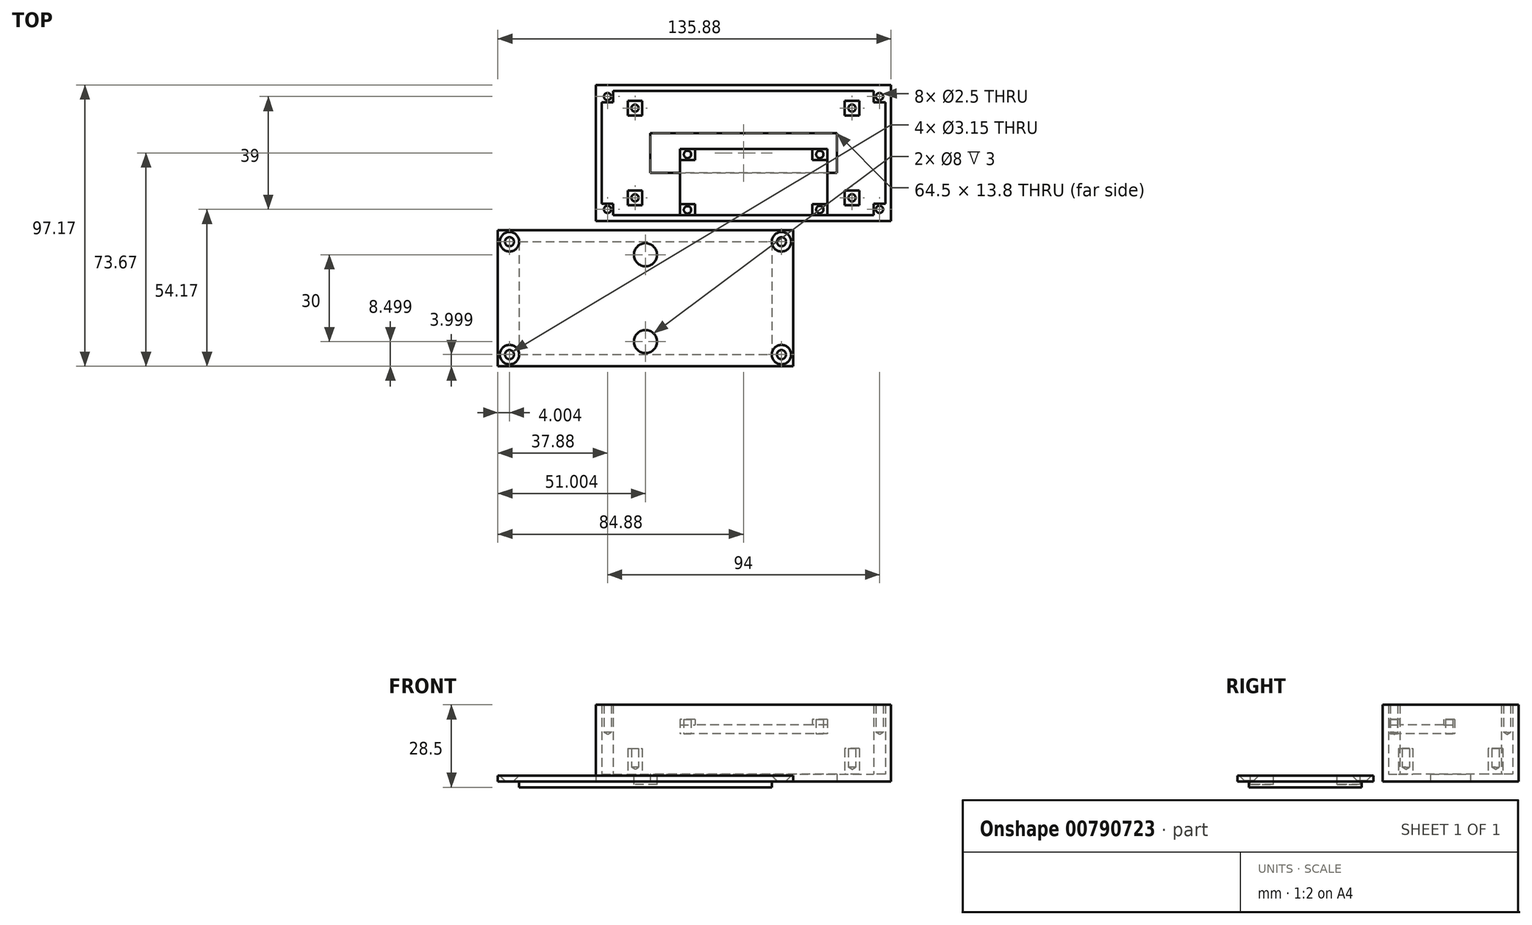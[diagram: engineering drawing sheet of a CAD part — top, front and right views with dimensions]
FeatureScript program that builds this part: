
annotation { "Feature Type Name" : "Feature", "Feature Type Description" : "" }
export const myFeature = defineFeature(function(context is Context, id is Id, definition is map)
    precondition{}
    {
        {
            var Q0;
            Q0=qCreatedBy(makeId("Top.planeOp"),FACE);
            var sketch = newSketch(context, id + "F0", { "sketchPlane" : qUnion([Q0])});
            skLineSegment(sketch, "E0.bottom", {"start": v(-51, 23.5) * mm, "end": v(51, 23.5) * mm});
            skLineSegment(sketch, "E0.top", {"start": v(-51, -23.5) * mm, "end": v(51, -23.5) * mm});
            skLineSegment(sketch, "E0.left", {"start": v(-51, 23.5) * mm, "end": v(-51, -23.5) * mm});
            skLineSegment(sketch, "E0.right", {"start": v(51, 23.5) * mm, "end": v(51, -23.5) * mm});
            skPoint(sketch, "E0.middle", {"position": v(0, 0) * mm});
            skSolve(sketch);
        }
        {
            var Q0;
            Q0=makeQuery(id+"F0.imprint","IMPRINT",FACE,{"disambiguationData":[TD([[makeQuery(id+"F0.imprint","IMPRINT",EDGE,{"derivedFrom":sQuery(id+"F0.wireOp",EDGE,"E0.bottom")}),-1.0]])]});
            extrude(context, id + "F1", {"entities" : qUnion([Q0]), "depth" : 26.5 * mm, "offsetDistance" : 25 * mm});
        }
        {
            var Q0;
            Q0=makeQuery(id+"F1.opExtrude","CAP_FACE",FACE,{"disambiguationData":[OSD([sQuery(id+"F0.wireOp",EDGE,"E0.bottom"),sQuery(id+"F0.wireOp",EDGE,"E0.top"),sQuery(id+"F0.wireOp",EDGE,"E0.left"),sQuery(id+"F0.wireOp",EDGE,"E0.right")])],"isStart":false});
            var sketch = newSketch(context, id + "F2", { "sketchPlane" : qUnion([Q0])});
            skLineSegment(sketch, "E1.bottom", {"start": v(-49, 21.5) * mm, "end": v(49, 21.5) * mm});
            skLineSegment(sketch, "E1.top", {"start": v(-49, -21.5) * mm, "end": v(49, -21.5) * mm});
            skLineSegment(sketch, "E1.left", {"start": v(-49, 21.5) * mm, "end": v(-49, -21.5) * mm});
            skLineSegment(sketch, "E1.right", {"start": v(49, 21.5) * mm, "end": v(49, -21.5) * mm});
            skPoint(sketch, "E1.middle", {"position": v(0, 0) * mm});
            skSolve(sketch);
        }
        {
            var Q0;
            Q0=makeQuery(id+"F2.imprint","IMPRINT",FACE,{"disambiguationData":[TD([[makeQuery(id+"F2.imprint","IMPRINT",EDGE,{"derivedFrom":sQuery(id+"F2.wireOp",EDGE,"E1.bottom")}),-1.0]])]});
            extrude(context, id + "F3", {"entities" : qUnion([Q0]), "operationType" : NewBodyOperationType.REMOVE, "oppositeDirection" : true, "depth" : 24 * mm, "offsetDistance" : 25 * mm});
        }
        {
            var Q0;
            Q0=makeQuery(id+"F1.opExtrude","CAP_FACE",FACE,{"disambiguationData":[OSD([sQuery(id+"F0.wireOp",EDGE,"E0.bottom"),sQuery(id+"F0.wireOp",EDGE,"E0.top"),sQuery(id+"F0.wireOp",EDGE,"E0.left"),sQuery(id+"F0.wireOp",EDGE,"E0.right")])],"isStart":true});
            var sketch = newSketch(context, id + "F4", { "sketchPlane" : qUnion([Q0])});
            skLineSegment(sketch, "E2.bottom", {"start": v(-32.25, -6.9) * mm, "end": v(32.25, -6.9) * mm});
            skLineSegment(sketch, "E2.top", {"start": v(-32.25, 6.9) * mm, "end": v(32.25, 6.9) * mm});
            skLineSegment(sketch, "E2.left", {"start": v(-32.25, -6.9) * mm, "end": v(-32.25, 6.9) * mm});
            skLineSegment(sketch, "E2.right", {"start": v(32.25, -6.9) * mm, "end": v(32.25, 6.9) * mm});
            skPoint(sketch, "E2.middle", {"position": v(0, 0) * mm});
            skSolve(sketch);
        }
        {
            var Q0;
            Q0=makeQuery(id+"F4.imprint","IMPRINT",FACE,{"disambiguationData":[TD([[makeQuery(id+"F4.imprint","IMPRINT",EDGE,{"derivedFrom":sQuery(id+"F4.wireOp",EDGE,"E2.bottom")}),1.0]])]});
            extrude(context, id + "F5", {"entities" : qUnion([Q0]), "operationType" : NewBodyOperationType.REMOVE, "endBound" : BoundingType.THROUGH_ALL, "oppositeDirection" : true, "depth" : 25 * mm, "offsetDistance" : 25 * mm});
        }
        {
            var Q0;
            Q0=makeQuery(id+"F3.boolean.opBoolean","COPY",FACE,{"derivedFrom":makeQuery(id+"F3.opExtrude","CAP_FACE",FACE,{"disambiguationData":[OSD([sQuery(id+"F2.wireOp",EDGE,"E1.bottom"),sQuery(id+"F2.wireOp",EDGE,"E1.top"),sQuery(id+"F2.wireOp",EDGE,"E1.left"),sQuery(id+"F2.wireOp",EDGE,"E1.right")])],"isStart":false})});
            var sketch = newSketch(context, id + "F6", { "sketchPlane" : qUnion([Q0])});
            skLineSegment(sketch, "E3.bottom", {"start": v(-40, 18) * mm, "end": v(40, 18) * mm, "construction": true});
            skLineSegment(sketch, "E3.top", {"start": v(-40, -18) * mm, "end": v(40, -18) * mm, "construction": true});
            skLineSegment(sketch, "E3.left", {"start": v(-40, 18) * mm, "end": v(-40, -18) * mm, "construction": true});
            skLineSegment(sketch, "E3.right", {"start": v(40, 18) * mm, "end": v(40, -18) * mm, "construction": true});
            skPoint(sketch, "E3.middle", {"position": v(0, 0) * mm});
            skLineSegment(sketch, "E4.bottom", {"start": v(-40, -18) * mm, "end": v(-35, -18) * mm});
            skLineSegment(sketch, "E4.top", {"start": v(-40, -13) * mm, "end": v(-35, -13) * mm});
            skLineSegment(sketch, "E4.left", {"start": v(-40, -18) * mm, "end": v(-40, -13) * mm});
            skLineSegment(sketch, "E4.right", {"start": v(-35, -18) * mm, "end": v(-35, -13) * mm});
            skLineSegment(sketch, "E5.bottom", {"start": v(-40, 18) * mm, "end": v(-35, 18) * mm});
            skLineSegment(sketch, "E5.top", {"start": v(-40, 13) * mm, "end": v(-35, 13) * mm});
            skLineSegment(sketch, "E5.left", {"start": v(-40, 18) * mm, "end": v(-40, 13) * mm});
            skLineSegment(sketch, "E5.right", {"start": v(-35, 18) * mm, "end": v(-35, 13) * mm});
            skLineSegment(sketch, "E6.bottom", {"start": v(40, 18) * mm, "end": v(35, 18) * mm});
            skLineSegment(sketch, "E6.top", {"start": v(40, 13) * mm, "end": v(35, 13) * mm});
            skLineSegment(sketch, "E6.left", {"start": v(40, 18) * mm, "end": v(40, 13) * mm});
            skLineSegment(sketch, "E6.right", {"start": v(35, 18) * mm, "end": v(35, 13) * mm});
            skLineSegment(sketch, "E7.bottom", {"start": v(40, -18) * mm, "end": v(35, -18) * mm});
            skLineSegment(sketch, "E7.top", {"start": v(40, -13) * mm, "end": v(35, -13) * mm});
            skLineSegment(sketch, "E7.left", {"start": v(40, -18) * mm, "end": v(40, -13) * mm});
            skLineSegment(sketch, "E7.right", {"start": v(35, -18) * mm, "end": v(35, -13) * mm});
            skPoint(sketch, "E8.centerSnap0", {"position": v(-40, 15.5) * mm});
            skPoint(sketch, "E8.centerSnap1", {"position": v(-37.5, 18) * mm});
            skPoint(sketch, "E9.centerSnap0", {"position": v(-40, -15.5) * mm});
            skPoint(sketch, "E9.centerSnap1", {"position": v(-37.5, -13) * mm});
            skPoint(sketch, "E10.centerSnap0", {"position": v(35, -15.5) * mm});
            skPoint(sketch, "E10.centerSnap1", {"position": v(37.5, -13) * mm});
            skPoint(sketch, "E11.centerSnap0", {"position": v(37.5, 13) * mm});
            skPoint(sketch, "E11.centerSnap1", {"position": v(35, 15.5) * mm});
            skSolve(sketch);
        }
        {
            var Q0;
            Q0=makeQuery(id+"F6.imprint","IMPRINT",FACE,{"disambiguationData":[TD([[makeQuery(id+"F6.imprint","IMPRINT",EDGE,{"derivedFrom":sQuery(id+"F6.wireOp",EDGE,"E5.bottom")}),-1.0]])]});
            var Q1;
            Q1=makeQuery(id+"F6.imprint","IMPRINT",FACE,{"disambiguationData":[TD([[makeQuery(id+"F6.imprint","IMPRINT",EDGE,{"derivedFrom":sQuery(id+"F6.wireOp",EDGE,"E4.bottom")}),1.0]])]});
            var Q2;
            Q2=makeQuery(id+"F6.imprint","IMPRINT",FACE,{"disambiguationData":[TD([[makeQuery(id+"F6.imprint","IMPRINT",EDGE,{"derivedFrom":sQuery(id+"F6.wireOp",EDGE,"E7.bottom")}),-1.0]])]});
            var Q3;
            Q3=makeQuery(id+"F6.imprint","IMPRINT",FACE,{"disambiguationData":[TD([[makeQuery(id+"F6.imprint","IMPRINT",EDGE,{"derivedFrom":sQuery(id+"F6.wireOp",EDGE,"E6.bottom")}),1.0]])]});
            extrude(context, id + "F7", {"entities" : qUnion([Q0, Q1, Q2, Q3]), "operationType" : NewBodyOperationType.ADD, "depth" : 8.9 * mm, "offsetDistance" : 25 * mm});
        }
        {
            var Q0;
            Q0=makeQuery(id+"F7.opExtrude","CAP_FACE",FACE,{"disambiguationData":[OSD([sQuery(id+"F6.wireOp",EDGE,"E5.bottom"),sQuery(id+"F6.wireOp",EDGE,"E5.top"),sQuery(id+"F6.wireOp",EDGE,"E5.left"),sQuery(id+"F6.wireOp",EDGE,"E5.right")])],"isStart":false});
            var sketch = newSketch(context, id + "F8", { "sketchPlane" : qUnion([Q0])});
            skPoint(sketch, "E12", {"position": v(-37.5, 15.5) * mm});
            skPoint(sketch, "E12.positionSnap0", {"position": v(-40, 15.5) * mm});
            skPoint(sketch, "E12.positionSnap1", {"position": v(-37.5, 18) * mm});
            skSolve(sketch);
        }
        {
            var Q0;
            Q0=makeQuery(id+"F7.opExtrude","CAP_FACE",FACE,{"disambiguationData":[OSD([sQuery(id+"F6.wireOp",EDGE,"E4.bottom"),sQuery(id+"F6.wireOp",EDGE,"E4.top"),sQuery(id+"F6.wireOp",EDGE,"E4.left"),sQuery(id+"F6.wireOp",EDGE,"E4.right")])],"isStart":false});
            var sketch = newSketch(context, id + "F9", { "sketchPlane" : qUnion([Q0])});
            skPoint(sketch, "E13", {"position": v(-37.5, -15.5) * mm});
            skPoint(sketch, "E13.positionSnap0", {"position": v(-40, -15.5) * mm});
            skPoint(sketch, "E13.positionSnap1", {"position": v(-37.5, -13) * mm});
            skSolve(sketch);
        }
        {
            var Q0;
            Q0=makeQuery(id+"F7.opExtrude","CAP_FACE",FACE,{"disambiguationData":[OSD([sQuery(id+"F6.wireOp",EDGE,"E6.bottom"),sQuery(id+"F6.wireOp",EDGE,"E6.top"),sQuery(id+"F6.wireOp",EDGE,"E6.left"),sQuery(id+"F6.wireOp",EDGE,"E6.right")])],"isStart":false});
            var sketch = newSketch(context, id + "F10", { "sketchPlane" : qUnion([Q0])});
            skPoint(sketch, "E14", {"position": v(37.5, 15.5) * mm});
            skPoint(sketch, "E14.positionSnap0", {"position": v(35, 15.5) * mm});
            skPoint(sketch, "E14.positionSnap1", {"position": v(37.5, 18) * mm});
            skSolve(sketch);
        }
        {
            var Q0;
            Q0=makeQuery(id+"F7.opExtrude","CAP_FACE",FACE,{"disambiguationData":[OSD([sQuery(id+"F6.wireOp",EDGE,"E7.bottom"),sQuery(id+"F6.wireOp",EDGE,"E7.top"),sQuery(id+"F6.wireOp",EDGE,"E7.left"),sQuery(id+"F6.wireOp",EDGE,"E7.right")])],"isStart":false});
            var sketch = newSketch(context, id + "F11", { "sketchPlane" : qUnion([Q0])});
            skPoint(sketch, "E15", {"position": v(37.5, -15.5) * mm});
            skPoint(sketch, "E15.positionSnap0", {"position": v(35, -15.5) * mm});
            skPoint(sketch, "E15.positionSnap1", {"position": v(37.5, -13) * mm});
            skSolve(sketch);
        }
        {
            var Q0;
            Q0=sQuery(id+"F8.wireOp",VERTEX,"E12");
            var Q1;
            Q1=sQuery(id+"F9.wireOp",VERTEX,"E13");
            var Q2;
            Q2=sQuery(id+"F11.wireOp",VERTEX,"E15");
            var Q3;
            Q3=sQuery(id+"F10.wireOp",VERTEX,"E14");
            var Q4;
            Q4=makeQuery(id+"F1.opExtrude","SWEPT_BODY",BODY,{"disambiguationData":[OSD([sQuery(id+"F0.wireOp",EDGE,"E0.bottom"),sQuery(id+"F0.wireOp",EDGE,"E0.top"),sQuery(id+"F0.wireOp",EDGE,"E0.left"),sQuery(id+"F0.wireOp",EDGE,"E0.right")])]});
            hole(context, id + "F12", {"style" : HoleStyle.SIMPLE, "endStyle" : HoleEndStyle.BLIND, "standardTappedOrClearance" : lookupTablePath({ "standard" : "ISO", "engagement" : "75%", "pitch" : "0.5 mm", "size" : "M3", "type" : "Tapped" }), "standardBlindInLast" : lookupTablePath({ "standard" : "ISO", "engagement" : "75%", "pitch" : "0.5 mm", "size" : "M3", "type" : "Tapped" }), "holeDiameter" : 2.5 * mm, "majorDiameter" : 3 * mm, "showTappedDepth" : true, "holeDepth" : 6.5 * mm, "tappedDepth" : 5 * mm, "tapClearance" : 3, "locations" : qUnion([Q0, Q1, Q2, Q3]), "scope" : qUnion([Q4])});
        }
        {
            var Q0;
            Q0=makeQuery(id+"F3.boolean.opBoolean","COPY",FACE,{"derivedFrom":makeQuery(id+"F3.opExtrude","CAP_FACE",FACE,{"disambiguationData":[OSD([sQuery(id+"F2.wireOp",EDGE,"E1.bottom"),sQuery(id+"F2.wireOp",EDGE,"E1.top"),sQuery(id+"F2.wireOp",EDGE,"E1.left"),sQuery(id+"F2.wireOp",EDGE,"E1.right")])],"isStart":false})});
            var sketch = newSketch(context, id + "F13", { "sketchPlane" : qUnion([Q0])});
            skLineSegment(sketch, "E16.bottom", {"start": v(-49, -21.5) * mm, "end": v(-45, -21.5) * mm});
            skLineSegment(sketch, "E16.top", {"start": v(-49, -17.5) * mm, "end": v(-45, -17.5) * mm});
            skLineSegment(sketch, "E16.left", {"start": v(-49, -21.5) * mm, "end": v(-49, -17.5) * mm});
            skLineSegment(sketch, "E16.right", {"start": v(-45, -21.5) * mm, "end": v(-45, -17.5) * mm});
            skLineSegment(sketch, "E17.bottom", {"start": v(-49, 21.5) * mm, "end": v(-45, 21.5) * mm});
            skLineSegment(sketch, "E17.top", {"start": v(-49, 17.5) * mm, "end": v(-45, 17.5) * mm});
            skLineSegment(sketch, "E17.left", {"start": v(-49, 21.5) * mm, "end": v(-49, 17.5) * mm});
            skLineSegment(sketch, "E17.right", {"start": v(-45, 21.5) * mm, "end": v(-45, 17.5) * mm});
            skLineSegment(sketch, "E18.bottom", {"start": v(49, 21.5) * mm, "end": v(45, 21.5) * mm});
            skLineSegment(sketch, "E18.top", {"start": v(49, 17.5) * mm, "end": v(45, 17.5) * mm});
            skLineSegment(sketch, "E18.left", {"start": v(49, 21.5) * mm, "end": v(49, 17.5) * mm});
            skLineSegment(sketch, "E18.right", {"start": v(45, 21.5) * mm, "end": v(45, 17.5) * mm});
            skLineSegment(sketch, "E19.bottom", {"start": v(49, -21.5) * mm, "end": v(45, -21.5) * mm});
            skLineSegment(sketch, "E19.top", {"start": v(49, -17.5) * mm, "end": v(45, -17.5) * mm});
            skLineSegment(sketch, "E19.left", {"start": v(49, -21.5) * mm, "end": v(49, -17.5) * mm});
            skLineSegment(sketch, "E19.right", {"start": v(45, -21.5) * mm, "end": v(45, -17.5) * mm});
            skSolve(sketch);
        }
        {
            var Q0;
            Q0 = qSketchRegion(id + "F13", true);
            extrude(context, id + "F14", {"entities" : qUnion([Q0]), "operationType" : NewBodyOperationType.ADD, "depth" : 24 * mm, "offsetDistance" : 25 * mm});
        }
        {
            var Q0;
            Q0=makeQuery(id+"F14.boolean.opBoolean","MERGE",FACE,{"derivedFrom":[makeQuery(id+"F1.opExtrude","CAP_FACE",FACE,{"disambiguationData":[OSD([sQuery(id+"F0.wireOp",EDGE,"E0.bottom"),sQuery(id+"F0.wireOp",EDGE,"E0.top"),sQuery(id+"F0.wireOp",EDGE,"E0.left"),sQuery(id+"F0.wireOp",EDGE,"E0.right")])],"isStart":false}),makeQuery(id+"F14.opExtrude","CAP_FACE",FACE,{"disambiguationData":[OSD([sQuery(id+"F13.wireOp",EDGE,"E16.bottom"),sQuery(id+"F13.wireOp",EDGE,"E16.top"),sQuery(id+"F13.wireOp",EDGE,"E16.left"),sQuery(id+"F13.wireOp",EDGE,"E16.right")])],"isStart":false}),makeQuery(id+"F14.opExtrude","CAP_FACE",FACE,{"disambiguationData":[OSD([sQuery(id+"F13.wireOp",EDGE,"E17.bottom"),sQuery(id+"F13.wireOp",EDGE,"E17.top"),sQuery(id+"F13.wireOp",EDGE,"E17.left"),sQuery(id+"F13.wireOp",EDGE,"E17.right")])],"isStart":false}),makeQuery(id+"F14.opExtrude","CAP_FACE",FACE,{"disambiguationData":[OSD([sQuery(id+"F13.wireOp",EDGE,"E18.bottom"),sQuery(id+"F13.wireOp",EDGE,"E18.top"),sQuery(id+"F13.wireOp",EDGE,"E18.left"),sQuery(id+"F13.wireOp",EDGE,"E18.right")])],"isStart":false}),makeQuery(id+"F14.opExtrude","CAP_FACE",FACE,{"disambiguationData":[OSD([sQuery(id+"F13.wireOp",EDGE,"E19.bottom"),sQuery(id+"F13.wireOp",EDGE,"E19.top"),sQuery(id+"F13.wireOp",EDGE,"E19.left"),sQuery(id+"F13.wireOp",EDGE,"E19.right")])],"isStart":false})]});
            var sketch = newSketch(context, id + "F15", { "sketchPlane" : qUnion([Q0])});
            skCircle(sketch, "E20", {"center": v(-47, 19.5) * mm, "radius": 1 * mm});
            skPoint(sketch, "E20.centerSnap0", {"position": v(-47, 17.5) * mm});
            skPoint(sketch, "E20.centerSnap1", {"position": v(-45, 19.5) * mm});
            skPoint(sketch, "E21.centerSnap0", {"position": v(-47, -17.5) * mm});
            skPoint(sketch, "E21.centerSnap1", {"position": v(-45, -19.5) * mm});
            skCircle(sketch, "E22", {"center": v(47, 19.5) * mm, "radius": 1 * mm});
            skPoint(sketch, "E22.centerSnap0", {"position": v(45, 19.5) * mm});
            skPoint(sketch, "E22.centerSnap1", {"position": v(47, 17.5) * mm});
            skCircle(sketch, "E23", {"center": v(47, -19.5) * mm, "radius": 1 * mm});
            skPoint(sketch, "E23.centerSnap0", {"position": v(47, -17.5) * mm});
            skPoint(sketch, "E23.centerSnap1", {"position": v(45, -19.5) * mm});
            skCircle(sketch, "E24", {"center": v(-47, -19.5) * mm, "radius": 1 * mm});
            skSolve(sketch);
        }
        {
            var Q0;
            Q0=sQuery(id+"F15.wireOp",VERTEX,"E24.center");
            var Q1;
            Q1=sQuery(id+"F15.wireOp",VERTEX,"E20.center");
            var Q2;
            Q2=sQuery(id+"F15.wireOp",VERTEX,"E22.center");
            var Q3;
            Q3=sQuery(id+"F15.wireOp",VERTEX,"E23.center");
            var Q4;
            Q4=makeQuery(id+"F1.opExtrude","SWEPT_BODY",BODY,{"disambiguationData":[OSD([sQuery(id+"F0.wireOp",EDGE,"E0.bottom"),sQuery(id+"F0.wireOp",EDGE,"E0.top"),sQuery(id+"F0.wireOp",EDGE,"E0.left"),sQuery(id+"F0.wireOp",EDGE,"E0.right")])]});
            hole(context, id + "F16", {"style" : HoleStyle.SIMPLE, "endStyle" : HoleEndStyle.BLIND, "standardTappedOrClearance" : lookupTablePath({ "standard" : "ISO", "engagement" : "75%", "pitch" : "0.5 mm", "size" : "M3", "type" : "Tapped" }), "standardBlindInLast" : lookupTablePath({ "standard" : "ISO", "engagement" : "75%", "pitch" : "0.5 mm", "size" : "M3", "type" : "Tapped" }), "holeDiameter" : 2.5 * mm, "majorDiameter" : 3 * mm, "showTappedDepth" : true, "holeDepth" : 9.5 * mm, "tappedDepth" : 8 * mm, "tapClearance" : 3, "locations" : qUnion([Q0, Q1, Q2, Q3]), "scope" : qUnion([Q4])});
        }
        {
            var Q0;
            Q0=qCreatedBy(makeId("Top.planeOp"),FACE);
            var sketch = newSketch(context, id + "F17", { "sketchPlane" : qUnion([Q0])});
            skLineSegment(sketch, "E25.bottom", {"start": v(-84.88, -26.67) * mm, "end": v(17.12, -26.67) * mm});
            skLineSegment(sketch, "E25.top", {"start": v(-84.88, -73.67) * mm, "end": v(17.12, -73.67) * mm});
            skLineSegment(sketch, "E25.left", {"start": v(-84.88, -26.67) * mm, "end": v(-84.88, -73.67) * mm});
            skLineSegment(sketch, "E25.right", {"start": v(17.12, -26.67) * mm, "end": v(17.12, -73.67) * mm});
            skSolve(sketch);
        }
        {
            var Q0;
            Q0 = qSketchRegion(id + "F17", true);
            extrude(context, id + "F18", {"entities" : qUnion([Q0]), "depth" : 2 * mm, "offsetDistance" : 25 * mm});
        }
        {
            var Q0;
            Q0=makeQuery(id+"F18.opExtrude","CAP_FACE",FACE,{"disambiguationData":[OSD([sQuery(id+"F17.wireOp",EDGE,"E25.bottom"),sQuery(id+"F17.wireOp",EDGE,"E25.top"),sQuery(id+"F17.wireOp",EDGE,"E25.left"),sQuery(id+"F17.wireOp",EDGE,"E25.right")])],"isStart":false});
            var sketch = newSketch(context, id + "F19", { "sketchPlane" : qUnion([Q0])});
            skLineSegment(sketch, "E26", {"start": v(-80.88, -26.67) * mm, "end": v(-80.88, -73.67) * mm, "construction": true});
            skLineSegment(sketch, "E27", {"start": v(13.12, -73.67) * mm, "end": v(13.12, -26.67) * mm, "construction": true});
            skLineSegment(sketch, "E28", {"start": v(-84.88, -30.67) * mm, "end": v(17.12, -30.67) * mm, "construction": true});
            skLineSegment(sketch, "E29", {"start": v(-84.88, -69.67) * mm, "end": v(17.12, -69.67) * mm, "construction": true});
            skPoint(sketch, "E30", {"position": v(-80.88, -30.67) * mm});
            skPoint(sketch, "E31", {"position": v(-80.88, -69.67) * mm});
            skPoint(sketch, "E32", {"position": v(13.12, -69.67) * mm});
            skPoint(sketch, "E33", {"position": v(13.12, -30.67) * mm});
            skSolve(sketch);
        }
        {
            var Q0;
            Q0=sQuery(id+"F19.wireOp",VERTEX,"E30");
            var Q1;
            Q1=sQuery(id+"F19.wireOp",VERTEX,"E31");
            var Q2;
            Q2=sQuery(id+"F19.wireOp",VERTEX,"E32");
            var Q3;
            Q3=sQuery(id+"F19.wireOp",VERTEX,"E33");
            var Q4;
            Q4=makeQuery(id+"F18.opExtrude","SWEPT_BODY",BODY,{"disambiguationData":[OSD([sQuery(id+"F17.wireOp",EDGE,"E25.bottom"),sQuery(id+"F17.wireOp",EDGE,"E25.top"),sQuery(id+"F17.wireOp",EDGE,"E25.left"),sQuery(id+"F17.wireOp",EDGE,"E25.right")])]});
            hole(context, id + "F20", {"style" : HoleStyle.C_SINK, "endStyle" : HoleEndStyle.THROUGH, "standardTappedOrClearance" : lookupTablePath({ "standard" : "ISO", "fit" : "Close", "size" : "M3", "type" : "Clearance" }), "standardBlindInLast" : lookupTablePath({ "fit" : "Close", "standard" : "ISO", "size" : "M3", "type" : "Clearance" }), "holeDiameter" : 3.15 * mm, "cSinkDiameter" : 6.72 * mm, "cSinkAngle" : 90 * degree, "majorDiameter" : 3 * mm, "isTappedThrough" : true, "tappedDepth" : 5 * mm, "tapClearance" : 3, "locations" : qUnion([Q0, Q1, Q2, Q3]), "scope" : qUnion([Q4])});
        }
        {
            var Q0;
            Q0=makeQuery(id+"F18.opExtrude","CAP_FACE",FACE,{"disambiguationData":[OSD([sQuery(id+"F17.wireOp",EDGE,"E25.bottom"),sQuery(id+"F17.wireOp",EDGE,"E25.top"),sQuery(id+"F17.wireOp",EDGE,"E25.left"),sQuery(id+"F17.wireOp",EDGE,"E25.right")])],"isStart":false});
            var sketch = newSketch(context, id + "F21", { "sketchPlane" : qUnion([Q0])});
            skPoint(sketch, "E34", {"position": v(-77.52, -69.67) * mm});
            skPoint(sketch, "E35", {"position": v(-77.52, -30.67) * mm});
            skPoint(sketch, "E36", {"position": v(9.76, -30.67) * mm});
            skPoint(sketch, "E37", {"position": v(9.76, -69.67) * mm});
            skLineSegment(sketch, "E38.bottom", {"start": v(-77.52, -30.67) * mm, "end": v(9.76, -30.67) * mm});
            skLineSegment(sketch, "E38.top", {"start": v(-77.52, -69.67) * mm, "end": v(9.76, -69.67) * mm});
            skLineSegment(sketch, "E38.left", {"start": v(-77.52, -30.67) * mm, "end": v(-77.52, -69.67) * mm});
            skLineSegment(sketch, "E38.right", {"start": v(9.76, -30.67) * mm, "end": v(9.76, -69.67) * mm});
            skSolve(sketch);
        }
        {
            var Q0;
            Q0=makeQuery(id+"F21.imprint","IMPRINT",FACE,{"disambiguationData":[TD([[makeQuery(id+"F21.imprint","IMPRINT",EDGE,{"derivedFrom":sQuery(id+"F21.wireOp",EDGE,"E38.bottom")}),-1.0]])]});
            extrude(context, id + "F22", {"entities" : qUnion([Q0]), "operationType" : NewBodyOperationType.ADD, "oppositeDirection" : true, "depth" : 4 * mm, "offsetDistance" : 25 * mm});
        }
        {
            var Q0;
            Q0=makeQuery(id+"F18.opExtrude","CAP_FACE",FACE,{"disambiguationData":[OSD([sQuery(id+"F17.wireOp",EDGE,"E25.bottom"),sQuery(id+"F17.wireOp",EDGE,"E25.top"),sQuery(id+"F17.wireOp",EDGE,"E25.left"),sQuery(id+"F17.wireOp",EDGE,"E25.right")])],"isStart":false});
            var sketch = newSketch(context, id + "F23", { "sketchPlane" : qUnion([Q0])});
            skPoint(sketch, "E39", {"position": v(-33.88, -35.17) * mm});
            skPoint(sketch, "E39.positionSnap0", {"position": v(-33.88, -26.67) * mm});
            skPoint(sketch, "E40", {"position": v(-33.88, -73.67) * mm});
            skPoint(sketch, "E41", {"position": v(-33.88, -65.17) * mm});
            skCircle(sketch, "E42", {"center": v(-33.88, -35.17) * mm, "radius": 4 * mm});
            skCircle(sketch, "E43", {"center": v(-33.88, -65.17) * mm, "radius": 4 * mm});
            skSolve(sketch);
        }
        {
            var Q0;
            Q0=makeQuery(id+"F23.imprint","IMPRINT",FACE,{"disambiguationData":[TD([[makeQuery(id+"F23.imprint","IMPRINT",EDGE,{"derivedFrom":sQuery(id+"F23.wireOp",EDGE,"E42")}),1.0]])]});
            var Q1;
            Q1=makeQuery(id+"F23.imprint","IMPRINT",FACE,{"disambiguationData":[TD([[makeQuery(id+"F23.imprint","IMPRINT",EDGE,{"derivedFrom":sQuery(id+"F23.wireOp",EDGE,"E43")}),1.0]])]});
            extrude(context, id + "F24", {"entities" : qUnion([Q0, Q1]), "operationType" : NewBodyOperationType.REMOVE, "oppositeDirection" : true, "depth" : 3 * mm, "offsetDistance" : 25 * mm});
        }
        {
            var Q0;
            Q0=makeQuery(id+"F3.boolean.opBoolean","COPY",FACE,{"derivedFrom":makeQuery(id+"F3.opExtrude","SWEPT_FACE",FACE,{"disambiguationData":[OSD([sQuery(id+"F2.wireOp",EDGE,"E1.top")])]})});
            var sketch = newSketch(context, id + "F25", { "sketchPlane" : qUnion([Q0])});
            skLineSegment(sketch, "E44.bottom", {"start": v(-29, 19.5) * mm, "end": v(22, 19.5) * mm});
            skLineSegment(sketch, "E44.top", {"start": v(-29, 16.5) * mm, "end": v(22, 16.5) * mm});
            skLineSegment(sketch, "E44.left", {"start": v(-29, 19.5) * mm, "end": v(-29, 16.5) * mm});
            skLineSegment(sketch, "E44.right", {"start": v(22, 19.5) * mm, "end": v(22, 16.5) * mm});
            skSolve(sketch);
        }
        {
            var Q0;
            Q0=makeQuery(id+"F25.imprint","IMPRINT",FACE,{"disambiguationData":[TD([[makeQuery(id+"F25.imprint","IMPRINT",EDGE,{"derivedFrom":sQuery(id+"F25.wireOp",EDGE,"E44.bottom")}),-1.0]])]});
            var Q1;
            Q1 = qSketchRegion(id + "F27", true);
            extrude(context, id + "F26", {"entities" : qUnion([Q0, Q1]), "operationType" : NewBodyOperationType.ADD, "depth" : 22.86 * mm, "offsetDistance" : 25 * mm});
        }
        {
            var Q0;
            Q0=makeQuery(id+"F26.opExtrude","SWEPT_FACE",FACE,{"disambiguationData":[OSD([sQuery(id+"F25.wireOp",EDGE,"E44.bottom")])]});
            var sketch = newSketch(context, id + "F27", { "sketchPlane" : qUnion([Q0])});
            skPoint(sketch, "E45", {"position": v(26.36, -19.6) * mm});
            skPoint(sketch, "E46", {"position": v(26.36, -0.55) * mm});
            skPoint(sketch, "E47", {"position": v(-19.36, -0.55) * mm});
            skPoint(sketch, "E48", {"position": v(-19.36, -19.6) * mm});
            skLineSegment(sketch, "E49.bottom", {"start": v(29, -21.5) * mm, "end": v(23.72, -21.5) * mm});
            skLineSegment(sketch, "E49.top", {"start": v(29, -17.65) * mm, "end": v(23.72, -17.65) * mm});
            skLineSegment(sketch, "E49.left", {"start": v(29, -21.5) * mm, "end": v(29, -17.65) * mm});
            skLineSegment(sketch, "E49.right", {"start": v(23.72, -21.5) * mm, "end": v(23.72, -17.65) * mm});
            skLineSegment(sketch, "E50.bottom", {"start": v(29, -2.45) * mm, "end": v(23.72, -2.45) * mm});
            skLineSegment(sketch, "E50.top", {"start": v(29, 1.36) * mm, "end": v(23.72, 1.36) * mm});
            skLineSegment(sketch, "E50.left", {"start": v(29, -2.45) * mm, "end": v(29, 1.36) * mm});
            skLineSegment(sketch, "E50.right", {"start": v(23.72, -2.45) * mm, "end": v(23.72, 1.36) * mm});
            skLineSegment(sketch, "E51.bottom", {"start": v(-16.72, -21.5) * mm, "end": v(-22, -21.5) * mm});
            skLineSegment(sketch, "E51.top", {"start": v(-16.72, -17.7) * mm, "end": v(-22, -17.7) * mm});
            skLineSegment(sketch, "E51.left", {"start": v(-16.72, -21.5) * mm, "end": v(-16.72, -17.7) * mm});
            skLineSegment(sketch, "E51.right", {"start": v(-22, -21.5) * mm, "end": v(-22, -17.7) * mm});
            skLineSegment(sketch, "E52.bottom", {"start": v(-22, -2.45) * mm, "end": v(-16.72, -2.45) * mm});
            skLineSegment(sketch, "E52.top", {"start": v(-22, 1.36) * mm, "end": v(-16.72, 1.36) * mm});
            skLineSegment(sketch, "E52.left", {"start": v(-22, -2.45) * mm, "end": v(-22, 1.36) * mm});
            skLineSegment(sketch, "E52.right", {"start": v(-16.72, -2.45) * mm, "end": v(-16.72, 1.36) * mm});
            skSolve(sketch);
        }
        {
            var Q0;
            Q0=makeQuery(id+"F27.imprint","IMPRINT",FACE,{"disambiguationData":[TD([[makeQuery(id+"F27.imprint","IMPRINT",EDGE,{"derivedFrom":sQuery(id+"F27.wireOp",EDGE,"E50.bottom")}),-1.0]])]});
            var Q1;
            Q1=makeQuery(id+"F27.imprint","IMPRINT",FACE,{"disambiguationData":[TD([[makeQuery(id+"F27.imprint","IMPRINT",EDGE,{"derivedFrom":sQuery(id+"F27.wireOp",EDGE,"E49.bottom")}),-1.0]])]});
            var Q2;
            Q2=makeQuery(id+"F27.imprint","IMPRINT",FACE,{"disambiguationData":[TD([[makeQuery(id+"F27.imprint","IMPRINT",EDGE,{"derivedFrom":sQuery(id+"F27.wireOp",EDGE,"E51.bottom")}),-1.0]])]});
            var Q3;
            Q3=makeQuery(id+"F27.imprint","IMPRINT",FACE,{"disambiguationData":[TD([[makeQuery(id+"F27.imprint","IMPRINT",EDGE,{"derivedFrom":sQuery(id+"F27.wireOp",EDGE,"E52.bottom")}),1.0]])]});
            var Q4;
            Q4 = qSketchRegion(id + "F29", true);
            extrude(context, id + "F28", {"entities" : qUnion([Q0, Q1, Q2, Q3, Q4]), "operationType" : NewBodyOperationType.ADD, "depth" : 2 * mm, "offsetDistance" : 25 * mm});
        }
        {
            var Q0;
            Q0=makeQuery(id+"F28.opExtrude","CAP_FACE",FACE,{"disambiguationData":[OSD([sQuery(id+"F27.wireOp",EDGE,"E50.bottom"),sQuery(id+"F27.wireOp",EDGE,"E50.top"),sQuery(id+"F27.wireOp",EDGE,"E50.left"),sQuery(id+"F27.wireOp",EDGE,"E50.right")])],"isStart":false});
            var sketch = newSketch(context, id + "F29", { "sketchPlane" : qUnion([Q0])});
            skPoint(sketch, "E53", {"position": v(26.36, -0.5) * mm});
            skSolve(sketch);
        }
        {
            var Q0;
            Q0=makeQuery(id+"F28.opExtrude","CAP_FACE",FACE,{"disambiguationData":[OSD([sQuery(id+"F27.wireOp",EDGE,"E49.bottom"),sQuery(id+"F27.wireOp",EDGE,"E49.top"),sQuery(id+"F27.wireOp",EDGE,"E49.left"),sQuery(id+"F27.wireOp",EDGE,"E49.right")])],"isStart":false});
            var sketch = newSketch(context, id + "F30", { "sketchPlane" : qUnion([Q0])});
            skPoint(sketch, "E54", {"position": v(26.36, -19.55) * mm});
            skSolve(sketch);
        }
        {
            var Q0;
            Q0=makeQuery(id+"F28.opExtrude","CAP_FACE",FACE,{"disambiguationData":[OSD([sQuery(id+"F27.wireOp",EDGE,"E51.bottom"),sQuery(id+"F27.wireOp",EDGE,"E51.top"),sQuery(id+"F27.wireOp",EDGE,"E51.left"),sQuery(id+"F27.wireOp",EDGE,"E51.right")])],"isStart":false});
            var sketch = newSketch(context, id + "F31", { "sketchPlane" : qUnion([Q0])});
            skPoint(sketch, "E55", {"position": v(-19.36, -19.64) * mm});
            skSolve(sketch);
        }
        {
            var Q0;
            Q0=makeQuery(id+"F28.opExtrude","CAP_FACE",FACE,{"disambiguationData":[OSD([sQuery(id+"F27.wireOp",EDGE,"E52.bottom"),sQuery(id+"F27.wireOp",EDGE,"E52.top"),sQuery(id+"F27.wireOp",EDGE,"E52.left"),sQuery(id+"F27.wireOp",EDGE,"E52.right")])],"isStart":false});
            var sketch = newSketch(context, id + "F32", { "sketchPlane" : qUnion([Q0])});
            skPoint(sketch, "E56", {"position": v(-19.36, -0.5) * mm});
            skSolve(sketch);
        }
        {
            var Q0;
            Q0=sQuery(id+"F29.wireOp",VERTEX,"E53");
            var Q1;
            Q1=sQuery(id+"F30.wireOp",VERTEX,"E54");
            var Q2;
            Q2=sQuery(id+"F32.wireOp",VERTEX,"E56");
            var Q3;
            Q3=sQuery(id+"F31.wireOp",VERTEX,"E55");
            var Q4;
            Q4=makeQuery(id+"F1.opExtrude","SWEPT_BODY",BODY,{"disambiguationData":[OSD([sQuery(id+"F0.wireOp",EDGE,"E0.bottom"),sQuery(id+"F0.wireOp",EDGE,"E0.top"),sQuery(id+"F0.wireOp",EDGE,"E0.left"),sQuery(id+"F0.wireOp",EDGE,"E0.right")])]});
            hole(context, id + "F33", {"style" : HoleStyle.SIMPLE, "endStyle" : HoleEndStyle.BLIND, "holeDiameter" : 2.54 * mm, "majorDiameter" : 5 * mm, "holeDepth" : 5 * mm, "tappedDepth" : 5 * mm, "tapClearance" : 3, "locations" : qUnion([Q0, Q1, Q2, Q3]), "scope" : qUnion([Q4])});
        }
    });
